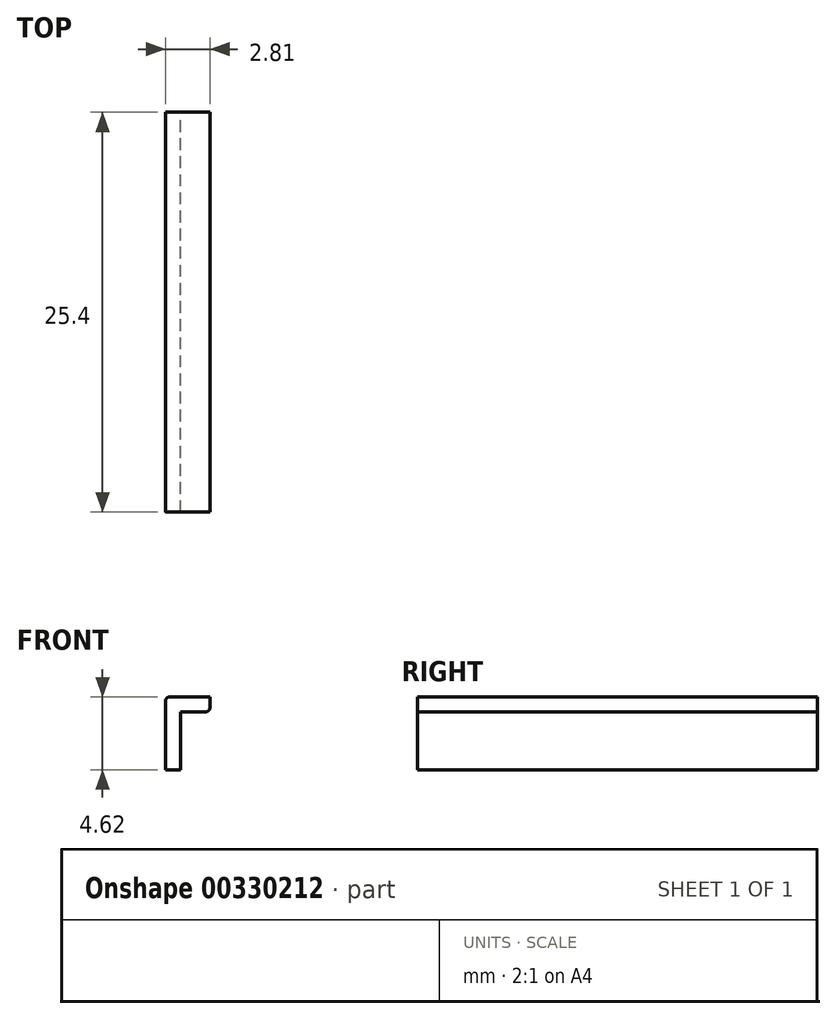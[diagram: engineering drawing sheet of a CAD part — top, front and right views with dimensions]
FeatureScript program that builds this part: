
annotation { "Feature Type Name" : "Feature", "Feature Type Description" : "" }
export const myFeature = defineFeature(function(context is Context, id is Id, definition is map)
    precondition{}
    {
        {
            var Q0;
            Q0=qCreatedBy(makeId("Front.planeOp"),FACE);
            var sketch = newSketch(context, id + "F0", { "sketchPlane" : qUnion([Q0])});
            skLineSegment(sketch, "E0.bottom", {"start": v(0.47, -1.84) * mm, "end": v(-0.47, -1.84) * mm});
            skLineSegment(sketch, "E0.top", {"start": v(0.47, 1.84) * mm, "end": v(-0.47, 1.84) * mm});
            skLineSegment(sketch, "E0.left", {"start": v(0.47, -1.84) * mm, "end": v(0.47, 1.84) * mm});
            skLineSegment(sketch, "E0.right", {"start": v(-0.47, -1.84) * mm, "end": v(-0.47, 1.84) * mm});
            skPoint(sketch, "E0.middle", {"position": v(0, 0) * mm});
            skLineSegment(sketch, "E1.bottom", {"start": v(-0.47, 1.84) * mm, "end": v(2.34, 1.84) * mm});
            skLineSegment(sketch, "E1.top", {"start": v(-0.47, 2.78) * mm, "end": v(2.34, 2.78) * mm});
            skLineSegment(sketch, "E1.left", {"start": v(-0.47, 1.84) * mm, "end": v(-0.47, 2.78) * mm});
            skLineSegment(sketch, "E1.right", {"start": v(2.34, 1.84) * mm, "end": v(2.34, 2.78) * mm});
            skLineSegment(sketch, "E2.bottom", {"start": v(2.34, 2.78) * mm, "end": v(1.4, 2.78) * mm});
            skLineSegment(sketch, "E2.top", {"start": v(2.34, 21.23) * mm, "end": v(1.4, 21.23) * mm});
            skLineSegment(sketch, "E2.left", {"start": v(2.34, 2.78) * mm, "end": v(2.34, 21.23) * mm});
            skLineSegment(sketch, "E2.right", {"start": v(1.4, 2.78) * mm, "end": v(1.4, 21.23) * mm});
            skSolve(sketch);
        }
        {
            var Q0;
            Q0=makeQuery(id+"F0.imprint","IMPRINT",FACE,{"disambiguationData":[TD([[makeQuery(id+"F0.imprint","IMPRINT",EDGE,{"derivedFrom":sQuery(id+"F0.wireOp",EDGE,"E2.bottom")}),-1.0]])]});
            var Q1;
            Q1=makeQuery(id+"F0.imprint","IMPRINT",FACE,{"disambiguationData":[TD([[makeQuery(id+"F0.imprint","IMPRINT",EDGE,{"derivedFrom":sQuery(id+"F0.wireOp",EDGE,"E1.top")}),-1.0]])]});
            var Q2;
            Q2=makeQuery(id+"F0.imprint","IMPRINT",FACE,{"disambiguationData":[TD([[makeQuery(id+"F0.imprint","IMPRINT",EDGE,{"derivedFrom":sQuery(id+"F0.wireOp",EDGE,"E0.bottom")}),-1.0]])]});
            extrude(context, id + "F1", {"entities" : qUnion([Q0, Q1, Q2]), "depth" : 25.4 * mm});
        }
        {
            var Q0;
            Q0=makeQuery(id+"F1.opExtrude","SWEPT_EDGE",EDGE,{"disambiguationData":[OSD([sQuery(id+"F0.wireOp",EDGE,"E1.top"),sQuery(id+"F0.wireOp",EDGE,"E2.bottom"),sQuery(id+"F0.wireOp",EDGE,"E2.right")])]});
            var Q1;
            Q1=makeQuery(id+"F1.opExtrude","SWEPT_EDGE",EDGE,{"disambiguationData":[OSD([sQuery(id+"F0.wireOp",EDGE,"E1.top"),sQuery(id+"F0.wireOp",EDGE,"E1.left")])]});
            var Q2;
            Q2=makeQuery(id+"F1.opExtrude","SWEPT_EDGE",EDGE,{"disambiguationData":[OSD([sQuery(id+"F0.wireOp",EDGE,"E1.bottom"),sQuery(id+"F0.wireOp",EDGE,"E1.right")])]});
            fillet(context, id + "F2", {"entities" : qUnion([Q0, Q1, Q2]), "radius" : 0.25 * mm, "tangentPropagation" : true, "allowEdgeOverflow" : false});
        }
    });
